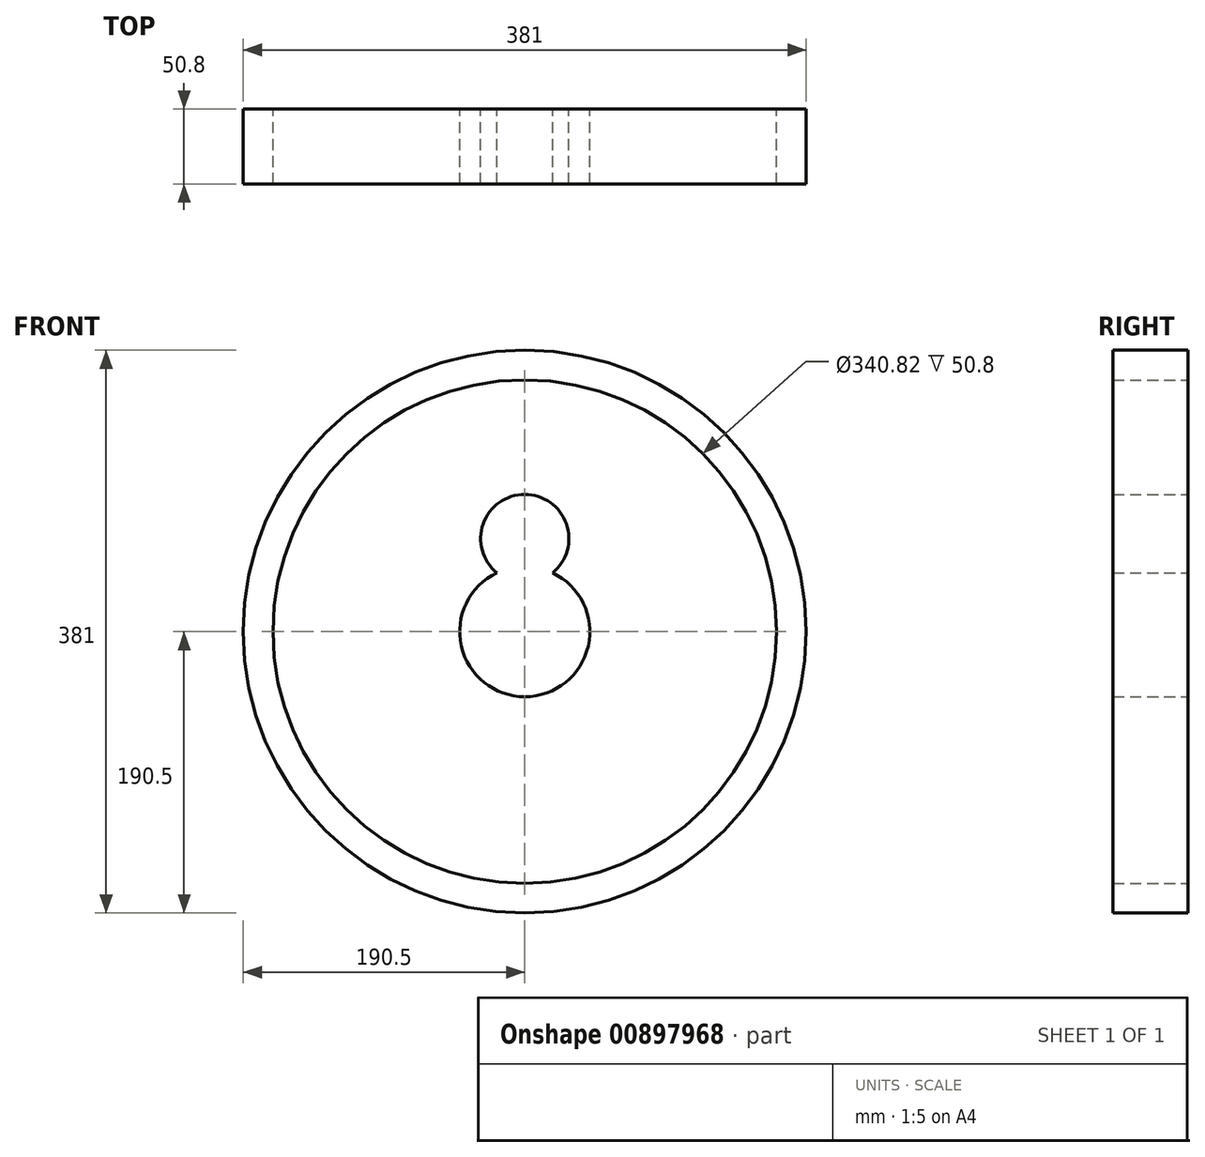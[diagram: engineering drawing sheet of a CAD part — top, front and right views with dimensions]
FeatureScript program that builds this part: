
annotation { "Feature Type Name" : "Feature", "Feature Type Description" : "" }
export const myFeature = defineFeature(function(context is Context, id is Id, definition is map)
    precondition{}
    {
        {
            var Q0;
            Q0=qCreatedBy(makeId("Front.planeOp"),FACE);
            var sketch = newSketch(context, id + "F0", { "sketchPlane" : qUnion([Q0])});
            skCircle(sketch, "E0", {"center": v(0, 0) * mm, "radius": 190.5 * mm});
            skCircle(sketch, "E1", {"center": v(0, 0) * mm, "radius": 170.41 * mm});
            skArc(sketch, "E2", {"start": v(-18.86, 39.8) * mm, "mid": v(0, -44.04) * mm, "end": v(18.86, 39.8) * mm});
            skArc(sketch, "E3", {"start": v(18.86, 39.8) * mm, "mid": v(0, 92.87) * mm, "end": v(-18.86, 39.8) * mm});
            skSolve(sketch);
        }
        {
            var Q0;
            Q0=makeQuery(id+"F0.imprint","IMPRINT",FACE,{"disambiguationData":[TD([[makeQuery(id+"F0.imprint","IMPRINT",EDGE,{"derivedFrom":sQuery(id+"F0.wireOp",EDGE,"E0")}),1.0]])]});
            var Q1;
            Q1=makeQuery(id+"F0.imprint","IMPRINT",FACE,{"disambiguationData":[TD([[makeQuery(id+"F0.imprint","IMPRINT",EDGE,{"derivedFrom":sQuery(id+"F0.wireOp",EDGE,"E2")}),1.0]])]});
            extrude(context, id + "F1", {"entities" : qUnion([Q0, Q1]), "depth" : 50.8 * mm, "offsetDistance" : 25.4 * mm});
        }
    });
